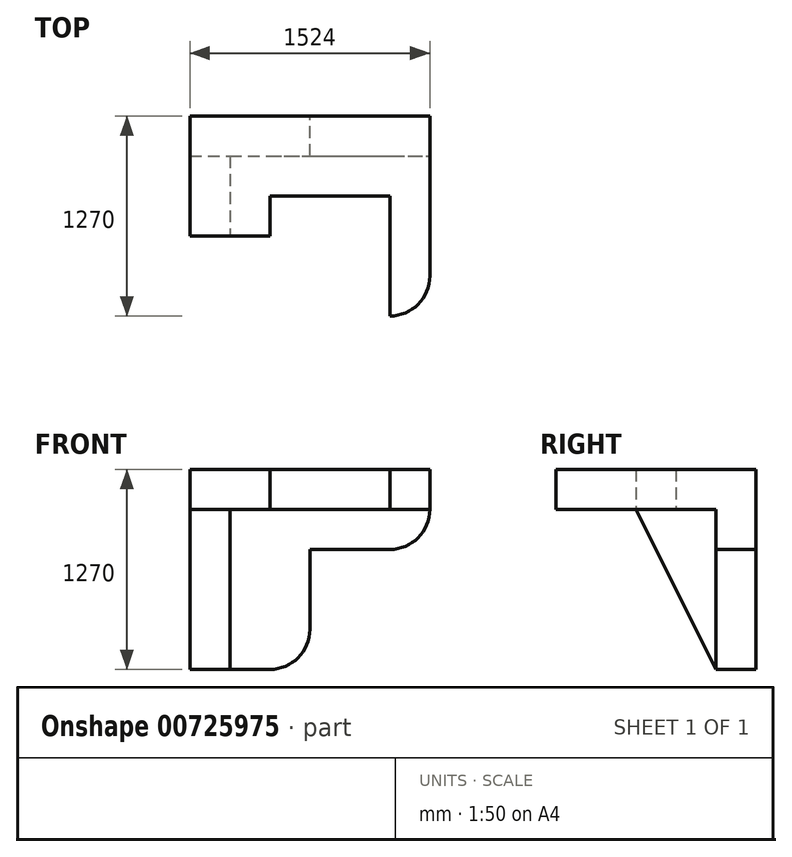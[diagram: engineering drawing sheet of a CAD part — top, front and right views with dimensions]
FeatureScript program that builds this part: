
annotation { "Feature Type Name" : "Feature", "Feature Type Description" : "" }
export const myFeature = defineFeature(function(context is Context, id is Id, definition is map)
    precondition{}
    {
        {
            var Q0;
            Q0=qCreatedBy(makeId("Front.planeOp"),FACE);
            var sketch = newSketch(context, id + "F0", { "sketchPlane" : qUnion([Q0])});
            skLineSegment(sketch, "E0", {"start": v(0, 0) * mm, "end": v(762, 0) * mm});
            skLineSegment(sketch, "E1", {"start": v(762, 0) * mm, "end": v(762, 762) * mm});
            skLineSegment(sketch, "E2", {"start": v(762, 762) * mm, "end": v(1524, 762) * mm});
            skLineSegment(sketch, "E3", {"start": v(1524, 762) * mm, "end": v(1524, 1270) * mm});
            skLineSegment(sketch, "E4", {"start": v(1524, 1270) * mm, "end": v(0, 1270) * mm});
            skLineSegment(sketch, "E5", {"start": v(0, 1270) * mm, "end": v(0, 0) * mm});
            skSolve(sketch);
        }
        {
            var Q0;
            Q0 = qSketchRegion(id + "F0", true);
            extrude(context, id + "F1", {"entities" : qUnion([Q0]), "depth" : 1270 * mm, "offsetDistance" : 25.4 * mm});
        }
        {
            var Q0;
            Q0=makeQuery(id+"F1.opExtrude","CAP_FACE",FACE,{"disambiguationData":[OSD([sQuery(id+"F0.wireOp",EDGE,"E0"),sQuery(id+"F0.wireOp",EDGE,"E1"),sQuery(id+"F0.wireOp",EDGE,"E2"),sQuery(id+"F0.wireOp",EDGE,"E3"),sQuery(id+"F0.wireOp",EDGE,"E4"),sQuery(id+"F0.wireOp",EDGE,"E5")])],"isStart":false});
            var sketch = newSketch(context, id + "F2", { "sketchPlane" : qUnion([Q0])});
            skLineSegment(sketch, "E6", {"start": v(762, 762) * mm, "end": v(254, 762) * mm});
            skLineSegment(sketch, "E7", {"start": v(254, 762) * mm, "end": v(254, 0) * mm});
            skLineSegment(sketch, "E8", {"start": v(254, 0) * mm, "end": v(762, 0) * mm});
            skLineSegment(sketch, "E9", {"start": v(762, 0) * mm, "end": v(762, 762) * mm});
            skSolve(sketch);
        }
        {
            var Q0;
            Q0 = qSketchRegion(id + "F2", true);
            extrude(context, id + "F3", {"entities" : qUnion([Q0]), "operationType" : NewBodyOperationType.REMOVE, "oppositeDirection" : true, "depth" : 1016 * mm, "offsetDistance" : 25.4 * mm});
        }
        {
            var Q0;
            Q0=makeQuery(id+"F1.opExtrude","CAP_FACE",FACE,{"disambiguationData":[OSD([sQuery(id+"F0.wireOp",EDGE,"E0"),sQuery(id+"F0.wireOp",EDGE,"E1"),sQuery(id+"F0.wireOp",EDGE,"E2"),sQuery(id+"F0.wireOp",EDGE,"E3"),sQuery(id+"F0.wireOp",EDGE,"E4"),sQuery(id+"F0.wireOp",EDGE,"E5")])],"isStart":false});
            var sketch = newSketch(context, id + "F4", { "sketchPlane" : qUnion([Q0])});
            skLineSegment(sketch, "E10", {"start": v(1524, 762) * mm, "end": v(254, 762) * mm});
            skLineSegment(sketch, "E11", {"start": v(254, 762) * mm, "end": v(254, 1016) * mm});
            skLineSegment(sketch, "E12", {"start": v(254, 1016) * mm, "end": v(1524, 1016) * mm});
            skLineSegment(sketch, "E13", {"start": v(1524, 1016) * mm, "end": v(1524, 762) * mm});
            skSolve(sketch);
        }
        {
            var Q0;
            Q0 = qSketchRegion(id + "F4", true);
            extrude(context, id + "F5", {"entities" : qUnion([Q0]), "operationType" : NewBodyOperationType.REMOVE, "oppositeDirection" : true, "depth" : 1016 * mm, "offsetDistance" : 25.4 * mm});
        }
        {
            var Q0;
            Q0=makeQuery(id+"F5.boolean.opBoolean","COPY",FACE,{"derivedFrom":makeQuery(id+"F5.opExtrude","SWEPT_FACE",FACE,{"disambiguationData":[OSD([sQuery(id+"F4.wireOp",EDGE,"E12")])]})});
            var sketch = newSketch(context, id + "F6", { "sketchPlane" : qUnion([Q0])});
            skLineSegment(sketch, "E14", {"start": v(508, 1270) * mm, "end": v(508, 508) * mm});
            skLineSegment(sketch, "E15", {"start": v(508, 508) * mm, "end": v(1270, 508) * mm});
            skLineSegment(sketch, "E16", {"start": v(1270, 508) * mm, "end": v(1270, 1270) * mm});
            skLineSegment(sketch, "E17", {"start": v(1270, 1270) * mm, "end": v(508, 1270) * mm});
            skSolve(sketch);
        }
        {
            var Q0;
            Q0 = qSketchRegion(id + "F6", true);
            extrude(context, id + "F7", {"entities" : qUnion([Q0]), "operationType" : NewBodyOperationType.REMOVE, "endBound" : BoundingType.THROUGH_ALL, "oppositeDirection" : true, "depth" : 25.4 * mm, "offsetDistance" : 25.4 * mm});
        }
        {
            var Q0;
            Q0=makeQuery(id+"F5.boolean.opBoolean","MERGE",FACE,{"derivedFrom":[makeQuery(id+"F3.boolean.opBoolean","COPY",FACE,{"derivedFrom":makeQuery(id+"F3.opExtrude","SWEPT_FACE",FACE,{"disambiguationData":[OSD([sQuery(id+"F2.wireOp",EDGE,"E7")])]})}),makeQuery(id+"F5.opExtrude","SWEPT_FACE",FACE,{"disambiguationData":[OSD([sQuery(id+"F4.wireOp",EDGE,"E11")])]})]});
            var sketch = newSketch(context, id + "F8", { "sketchPlane" : qUnion([Q0])});
            skLineSegment(sketch, "E18", {"start": v(-762, 0) * mm, "end": v(-762, 1016) * mm});
            skLineSegment(sketch, "E19", {"start": v(-762, 1016) * mm, "end": v(-1270, 1016) * mm});
            skLineSegment(sketch, "E20", {"start": v(-1270, 1016) * mm, "end": v(-1270, 0) * mm});
            skLineSegment(sketch, "E21", {"start": v(-1270, 0) * mm, "end": v(-762, 0) * mm});
            skSolve(sketch);
        }
        {
            var Q0;
            Q0 = qSketchRegion(id + "F8", true);
            extrude(context, id + "F9", {"entities" : qUnion([Q0]), "operationType" : NewBodyOperationType.REMOVE, "endBound" : BoundingType.THROUGH_ALL, "oppositeDirection" : true, "depth" : 25.4 * mm, "offsetDistance" : 25.4 * mm});
        }
        {
            var Q0;
            Q0=makeQuery(id+"F5.boolean.opBoolean","MERGE",FACE,{"derivedFrom":[makeQuery(id+"F3.boolean.opBoolean","COPY",FACE,{"derivedFrom":makeQuery(id+"F3.opExtrude","SWEPT_FACE",FACE,{"disambiguationData":[OSD([sQuery(id+"F2.wireOp",EDGE,"E7")])]})}),makeQuery(id+"F5.opExtrude","SWEPT_FACE",FACE,{"disambiguationData":[OSD([sQuery(id+"F4.wireOp",EDGE,"E11")])]})]});
            var sketch = newSketch(context, id + "F10", { "sketchPlane" : qUnion([Q0])});
            skLineSegment(sketch, "E22", {"start": v(-762, 1016) * mm, "end": v(-254, 0) * mm});
            skLineSegment(sketch, "E23", {"start": v(-254, 0) * mm, "end": v(-762, 0) * mm});
            skLineSegment(sketch, "E24", {"start": v(-762, 0) * mm, "end": v(-762, 1016) * mm});
            skSolve(sketch);
        }
        {
            var Q0;
            Q0 = qSketchRegion(id + "F10", true);
            extrude(context, id + "F11", {"entities" : qUnion([Q0]), "operationType" : NewBodyOperationType.REMOVE, "endBound" : BoundingType.THROUGH_ALL, "oppositeDirection" : true, "depth" : 25.4 * mm, "offsetDistance" : 25.4 * mm});
        }
        {
            var Q0;
            Q0=makeQuery(id+"F9.boolean.opBoolean","MERGE",FACE,{"derivedFrom":[makeQuery(id+"F5.boolean.opBoolean","COPY",FACE,{"derivedFrom":makeQuery(id+"F5.opExtrude","SWEPT_FACE",FACE,{"disambiguationData":[OSD([sQuery(id+"F4.wireOp",EDGE,"E12")])]})}),makeQuery(id+"F9.opExtrude","SWEPT_FACE",FACE,{"disambiguationData":[OSD([sQuery(id+"F8.wireOp",EDGE,"E19")])]})]});
            var sketch = newSketch(context, id + "F12", { "sketchPlane" : qUnion([Q0])});
            skLineSegment(sketch, "E25", {"start": v(0, 1270) * mm, "end": v(0, 762) * mm});
            skLineSegment(sketch, "E26", {"start": v(0, 762) * mm, "end": v(508, 762) * mm});
            skLineSegment(sketch, "E27", {"start": v(508, 762) * mm, "end": v(508, 1270) * mm});
            skLineSegment(sketch, "E28", {"start": v(508, 1270) * mm, "end": v(0, 1270) * mm});
            skSolve(sketch);
        }
        {
            var Q0;
            Q0 = qSketchRegion(id + "F12", true);
            extrude(context, id + "F13", {"entities" : qUnion([Q0]), "operationType" : NewBodyOperationType.REMOVE, "endBound" : BoundingType.THROUGH_ALL, "oppositeDirection" : true, "depth" : 25.4 * mm, "offsetDistance" : 25.4 * mm});
        }
        {
            var Q0;
            Q0=makeQuery(id+"F1.opExtrude","SWEPT_EDGE",EDGE,{"disambiguationData":[OSD([sQuery(id+"F0.wireOp",EDGE,"E0"),sQuery(id+"F0.wireOp",EDGE,"E1")])]});
            var Q1;
            Q1=makeQuery(id+"F1.opExtrude","SWEPT_EDGE",EDGE,{"disambiguationData":[OSD([sQuery(id+"F0.wireOp",EDGE,"E2"),sQuery(id+"F0.wireOp",EDGE,"E3")])]});
            fillet(context, id + "F14", {"entities" : qUnion([Q0, Q1]), "radius" : 254 * mm, "tangentPropagation" : true, "allowEdgeOverflow" : false});
        }
        {
            var Q0;
            Q0=makeQuery(id+"F1.opExtrude","CAP_EDGE",EDGE,{"disambiguationData":[OSD([sQuery(id+"F0.wireOp",EDGE,"E3")])],"isStart":false});
            fillet(context, id + "F15", {"entities" : qUnion([Q0]), "radius" : 254 * mm, "tangentPropagation" : true, "allowEdgeOverflow" : false});
        }
    });
